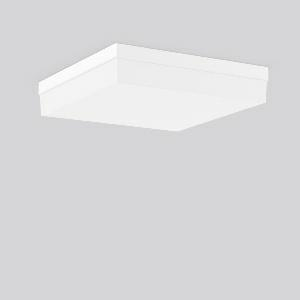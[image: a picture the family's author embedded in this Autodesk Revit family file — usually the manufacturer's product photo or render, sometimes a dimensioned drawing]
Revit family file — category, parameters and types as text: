
# Revit family: flat_quadrat_221162_002_045a
name_source: partatom
category: Lighting Fixtures
units: mm (PartAtom-declared; Revit-internal decimal feet)

## family parameters
Cut with Voids When Loaded = No
Host = Face
Light Source = No
Part Type = Normal
Room Calculation Point = No
Round Connector Dimension = Use Diameter
Shared = No

## types (1)
- FLAT QUADRAT (1 x LED Modul 830, 3500 lm, 3000)
    Apparent Load = 54 VA
    CIE Flux Codes = 42 72 91 88 100
    Color Rendering = 80
    Color Temperature = 3000
    Default Elevation = 1800 mm
    Description = Series: FLAT QUADRAT
Flat, square surface-mounted luminaire. Base: plastic. Diffuser: plastic (polypropylene), opal, satin finish. Diffuser fastening: spring system. IP 43 ceiling mounting, IP 44 wall mounting. 
Colour: white
Length: 470 mm
Width: 470 mm
Height: 100 mm
Lamp: LED
Socket: without socket
Colour temperature: 3000K
Colour rendering index (CRI): 83
System power: 54 W
Rated luminous flux: 3500 lm
Luminous efficiency: 65 lm/W
Control gear: Regulated power supply
Protection class: I
Type of protection: IP 43
    Height = 100 mm  [stored 0.328084 ft]
    Lamp = 1 x LED Modul 830
    Lamp Light Flux = 3500 lm
    Lamp count = 1
    Length = 470 mm
    Lifetime = 50000 h
    Luminous efficacy = 65 lm/W
    Manufacturer = RZB
    ModVariant = No
    Model = 221162.002
    Mounting Place = Ceiling, Wall
    Mounting Type = Surface mounted
    Number of Poles = 1
    OnlyDefault = Yes
    Power Factor = 1
    Product Name = FLAT QUADRAT
    Product group = Surface mounted ceiling and wall luminaires
    ProductGroupID = 305
    Protection Class = Protection class I
    Protection Degree = IP 43
    RLX_Detail_Level = 1
    RLX_Emergency_Light_Flux = 0 lm
    RLX_Emergency_Type = 0
    RLX_Emergency_Type_DB = No
    RlxData = <blob elided: 13953 chars, md5=0146651d>
    Socket = socket
    Standby Power = 0 W
    System Light Flux = 3500 lm
    System Power = 54 W
    Type Comments = Product without accessories
    Type Image = 221080.862.79.jpg
    URL = http://relux.com
    VarID = ---
    Voltage = 230 V
    Voltage Range = 220-240 V
    Weight = 0.00 kg
    Width = 470 mm

note: [stored X ft] marks values corroborated as IEEE doubles in the binary element streams (Revit-internal decimal feet)

## geometry (parser evidence)
native form markers: Sweep x12
no freeform markers — native parametric forms only
